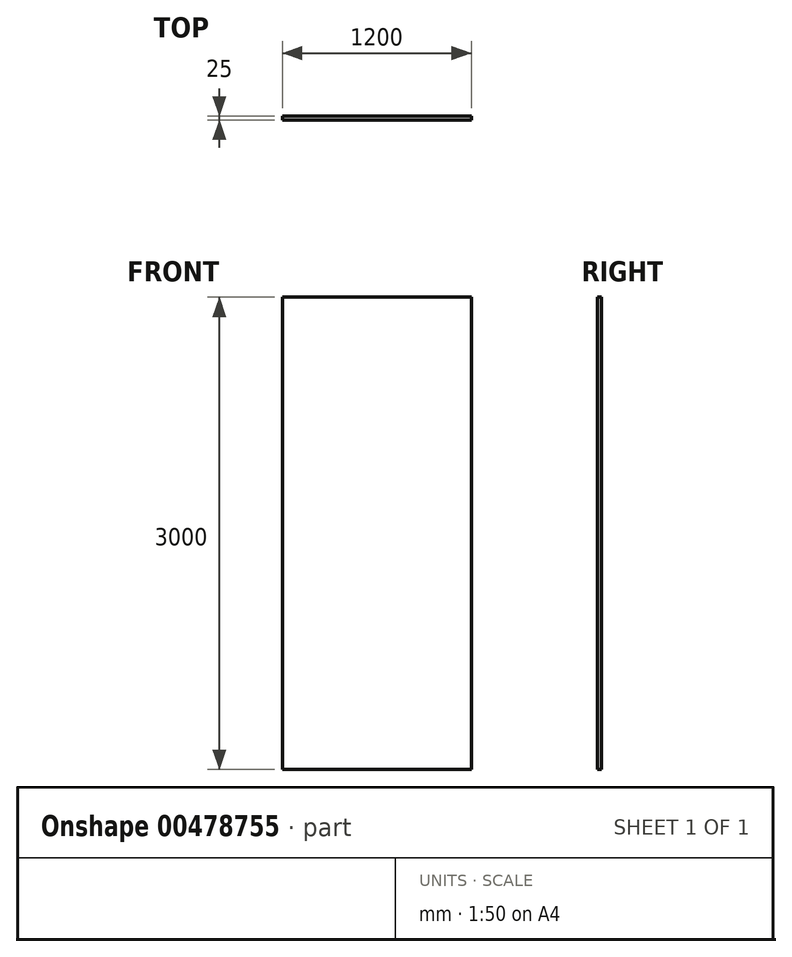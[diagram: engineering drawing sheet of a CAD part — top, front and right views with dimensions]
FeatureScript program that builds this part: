
annotation { "Feature Type Name" : "Feature", "Feature Type Description" : "" }
export const myFeature = defineFeature(function(context is Context, id is Id, definition is map)
    precondition{}
    {
        {
            var Q0;
            Q0=qCreatedBy(makeId("Front.planeOp"),FACE);
            var sketch = newSketch(context, id + "F0", { "sketchPlane" : qUnion([Q0])});
            skLineSegment(sketch, "E0.bottom", {"start": v(0, 0) * mm, "end": v(1200, 0) * mm});
            skLineSegment(sketch, "E0.top", {"start": v(0, 3000) * mm, "end": v(1200, 3000) * mm});
            skLineSegment(sketch, "E0.left", {"start": v(0, 0) * mm, "end": v(0, 3000) * mm});
            skLineSegment(sketch, "E0.right", {"start": v(1200, 0) * mm, "end": v(1200, 3000) * mm});
            skSolve(sketch);
        }
        {
            var Q0;
            Q0 = qSketchRegion(id + "F0", true);
            extrude(context, id + "F1", {"entities" : qUnion([Q0]), "depth" : 25 * mm});
        }
    });
